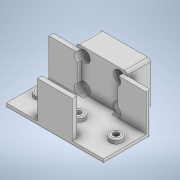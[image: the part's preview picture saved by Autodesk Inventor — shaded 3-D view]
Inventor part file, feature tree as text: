
AUTODESK INVENTOR PART (.ipt)
format: ipt  version: 2020 (Build 240168000, 168)  size: 345,600 bytes
history: native  units: in
note: dims shown in document units (in); Inventor stores cm internally (conversion verified against a paired STEP export)
features: extrude x16, sketch x16, fillet x3
ambient origin geometry x8: Origin, YZ Plane, XZ Plane, XY Plane, X Axis, Y Axis, Z Axis, Center Point
bodies: Solid1 (feature_tree)
feature tree (35):
  extrude  "Extrusion1"  Depth=1.2756in
  extrude  "Extrusion3"  Depth=0.1181in
  extrude  "Extrusion4"  Depth=1.0in TaperAngle=0.0deg
  extrude  "Extrusion5"  Depth=0.1181in TaperAngle=0.0deg
  extrude  "Extrusion6"  Depth=0.1181in TaperAngle=0.0deg
  extrude  "Extrusion9"  Depth=0.3346in
  extrude  "Extrusion10"  Depth=1.0236in
  extrude  "Extrusion11"  Depth=0.2953in
  extrude  "Extrusion14"  Depth=0.3346in
  fillet  "Fillet1"  Radius=0.1181in
  fillet  "Fillet2"  Radius=0.7677in
  extrude  "Extrusion15"  Depth=1.0in TaperAngle=0.0deg
  extrude  "Extrusion16"  Depth=0.0394in
  extrude  "Extrusion17"  Depth=0.1575in
  extrude  "Extrusion19"  Depth=0.1575in
  extrude  "Extrusion20"  Depth=0.3937in
  extrude  "Extrusion21"  Depth=0.2362in
  extrude  "Extrusion22"  Depth=1.378in
  fillet  "Fillet5"  Radius=1.1811in
  sketch  "Sketch1"  dims[d0=1.6142in d1=1.2756in]
  sketch  "Sketch3"  dims[d2=0.1181in d3=0.0in d8=0.1181in]
  sketch  "Sketch4"  dims[d9=0.1181in d10=1.0in d11=0.0in]
  sketch  "Sketch5"  dims[d12=0.8465in d13=0.1181in d14=0.0in]
  sketch  "Sketch6"  dims[d15=0.8465in d16=0.1181in d17=0.0in]
  sketch  "Sketch9"  dims[d20=0.3346in d21=0.3346in]
  sketch  "Sketch10"  dims[d22=0.1181in d23=0.0in d32=1.0236in]
  sketch  "Sketch11"  dims[d33=0.2953in d34=0.2953in]
  sketch  "Sketch14"  dims[d35=1.0236in d36=0.0in d37=0.3346in d38=0.1181in d39=0.0in d40=0.7677in]
  sketch  "Sketch15"  dims[d41=0.1181in d42=1.0in d43=0.0in]
  sketch  "Sketch16"  dims[d50=0.1772in d51=0.0in d52=0.0394in]
  sketch  "Sketch17"  dims[d53=0.0394in d54=0.1575in]
  sketch  "Sketch18"  dims[d55=0.1575in d56=0.1575in]
  sketch  "Sketch19"  dims[d57=0.3937in d58=0.0in d59=0.2362in]
  sketch  "Sketch20"  dims[d60=0.2362in d61=0.2362in]
  sketch  "Sketch21"  dims[d62=0.1181in d63=0.0in d64=1.378in d65=1.1811in d66=0.6299in d67=0.0in d68=1.378in d71=0.748in d72=0.0in d73=0.315in d74=0.315in d75=0.315in d76=0.315in d77=0.6299in d78=0.0in d79=0.3937in d80=0.3937in d81=0.3937in d82=0.3937in d83=0.2362in d84=0.0in d85=0.2165in d86=0.2165in d87=0.2165in d88=0.2165in d89=1.5748in d90=0.0in d93=0.0787in d44=0.0197in d45=0.0344in d94=0.0344in d95=0.0197in d96=0.0344in]
